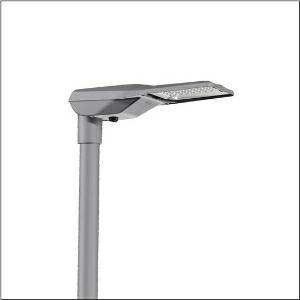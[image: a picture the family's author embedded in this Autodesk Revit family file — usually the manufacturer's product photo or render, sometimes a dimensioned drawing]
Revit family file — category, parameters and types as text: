
# Revit family: streetlight_sl_21_mini___st1_0a_5xe2d33r08gb_66de
name_source: partatom
category: Lighting Fixtures
units: mm (PartAtom-declared; Revit-internal decimal feet)

## family parameters
Cut with Voids When Loaded = No
Host = Face
Light Source = No
Part Type = Normal
Room Calculation Point = No
Round Connector Dimension = Use Diameter
Shared = No

## types (1)
- --- (1 x LED, 5940 lm, 40.4 W, 3000K)
    Apparent Load = 40 VA
    CIE Flux Codes = 37 72 97 100 100
    Color Rendering = 70
    Color Temperature = 3000K
    Default Elevation = 1800 mm
    Description = Streetlight SL 21 mini, mast luminaire, primary light control with lens, of PMMA, primary optical cover: cover, of toughened safety glass, transparent, light distribution: ST1.0a, light emission: direct distribution, primary light characteristic: asymmetric, installation type: side-entry, post-top, LED, High Power LED, rated luminous flux: 5.940lm, luminous efficacy: 147lm/W, light colour: 730, colour temperature: 3000K, control gear: D4i, control: flexible luminous flux parameterisation, time-dependent luminous flux control, constant luminous flux control, overheat protection, pre-setting: logarithmic dimming characteristic, mains connection: 220..240V, AC, 50/60Hz, start of lifetime: 40W, end of service life: 41W, reduction: 19W, luminaire housing, of diecast aluminium, powder-coated, SITECO metallic grey (DB 702S), corrosivity category C5 high according to DIN EN ISO 12944, please order mast flange separately, inclination adjustable: 0°, 5°, 10°, 15°, sealing non-destructively replaceable, multi-level sealing system, length: 628mm, width: 235mm, height: 110mm, mast flange for spigot size: 42mm (side-entry): 5XC10008XM4, 60/48mm (side-entry/post-top): 5XC10108XM2, 76/60mm (side-entry/post-top): 5XC10108XM1, mounting height: 4..8m, Smart Interface below, protection rating (complete): IP66, insulation class (complete): insulation class II (safety insulation), certification: CE, ENEC, ENEC+, VDE, impact resistance: IK10, permissible operating ambient temperature for outdoor applications: -40..+50°C, standard-compliant lighting for roads and squares, packaging unit: 1 piece

Light Distribution: ST1.0a
    Height = 110 mm
    Lamp = 1 x LED
    Lamp Light Flux = 5940 lm
    Lamp Power = 40.4 W
    Lamp count = 1
    Length = 625 mm
    Luminous efficacy = 147 lm/W
    Manufacturer = Siteco
    ModVariant = No
    Model = 5XE2D33R08GB
    Number of Poles = 1
    OnlyDefault = Yes
    Power Factor = 1
    Product Name = Streetlight SL 21 mini | ST1.0a
    Product group = mast luminaire | pylon top
    ProductGroupID = 6100
    Protection Class = Protection class II
    Protection Degree = IP 66
    RLX_Detail_Level = 1
    RLX_Emergency_Light_Flux = 0 lm
    RLX_Emergency_Type = 0
    RLX_Emergency_Type_DB = No
    RlxData = <blob elided: 26201 chars, md5=bab80cf4>
    Socket = socket
    Standby Power = 0 W
    System Light Flux = 5940 lm
    System Power = 40 W
    Type Comments = factory setting: luminous flux: 100 % | dim-lin: 254 | 812 mA
    Type Image = l_1003516.jpg
    URL = http://relux.com
    VarID = @adj_186267
    Voltage = 0 V
    Weight = 0.00 kg
    Width = 234 mm

## geometry (parser evidence)
native form markers: Blend x4, Sweep x12
no freeform markers — native parametric forms only
